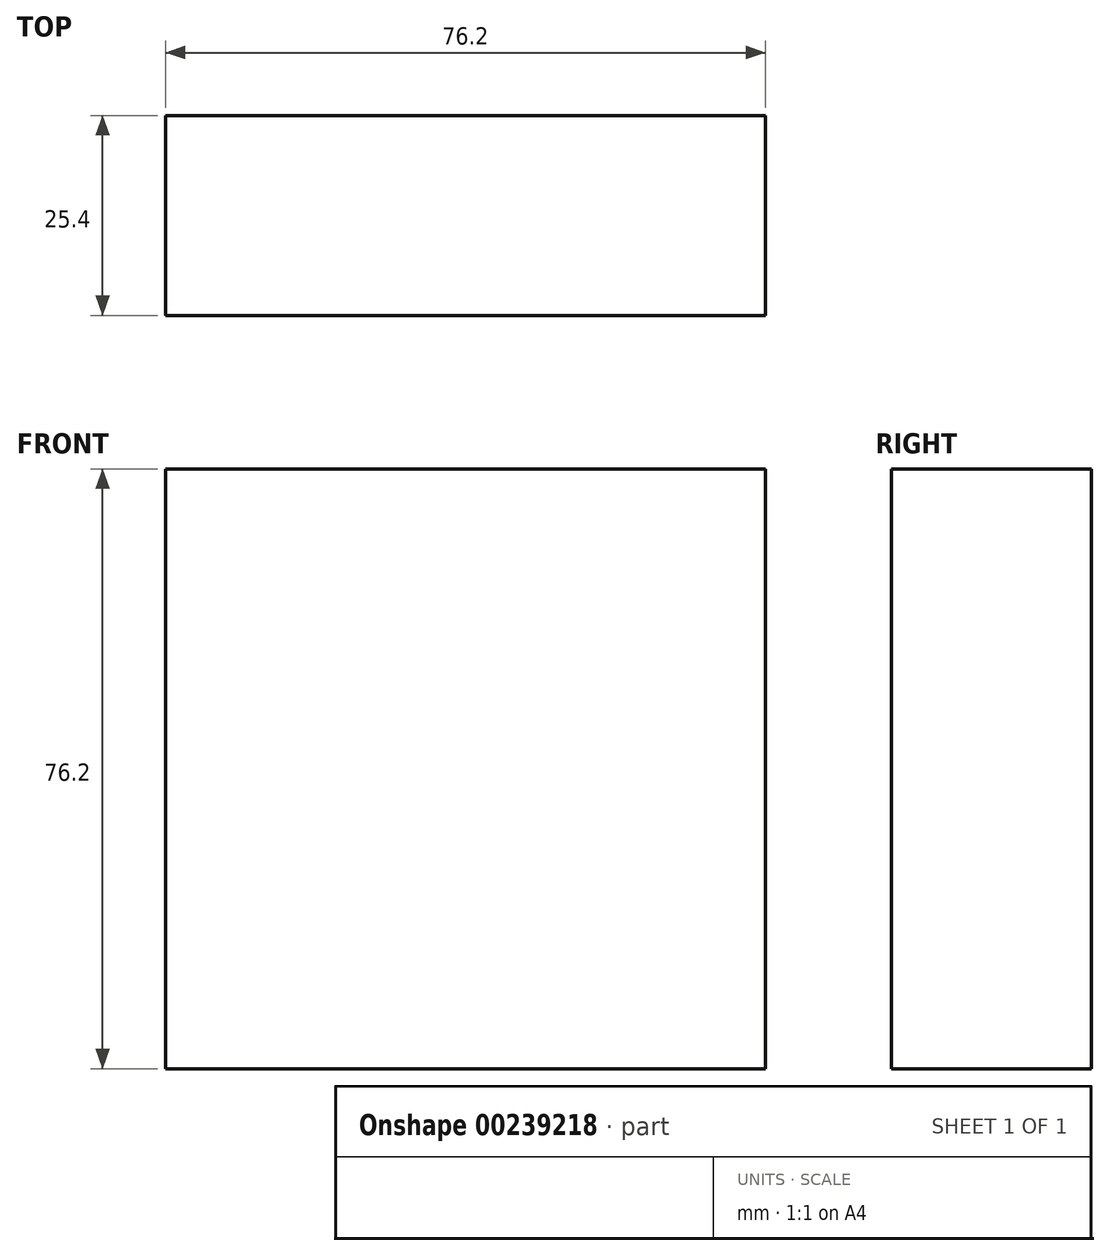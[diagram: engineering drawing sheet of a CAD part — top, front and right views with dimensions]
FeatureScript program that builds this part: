
annotation { "Feature Type Name" : "Feature", "Feature Type Description" : "" }
export const myFeature = defineFeature(function(context is Context, id is Id, definition is map)
    precondition{}
    {
        {
            var Q0;
            Q0=qCreatedBy(makeId("Front.planeOp"),FACE);
            var sketch = newSketch(context, id + "F0", { "sketchPlane" : qUnion([Q0])});
            skLineSegment(sketch, "E0.bottom", {"start": v(-38.1, 38.1) * mm, "end": v(38.1, 38.1) * mm});
            skLineSegment(sketch, "E0.top", {"start": v(-38.1, -38.1) * mm, "end": v(38.1, -38.1) * mm});
            skLineSegment(sketch, "E0.left", {"start": v(-38.1, 38.1) * mm, "end": v(-38.1, -38.1) * mm});
            skLineSegment(sketch, "E0.right", {"start": v(38.1, 38.1) * mm, "end": v(38.1, -38.1) * mm});
            skPoint(sketch, "E0.middle", {"position": v(0, 0) * mm});
            skSolve(sketch);
        }
        {
            var Q0;
            Q0 = qSketchRegion(id + "F0", true);
            extrude(context, id + "F1", {"entities" : qUnion([Q0]), "depth" : 25.4 * mm});
        }
    });
